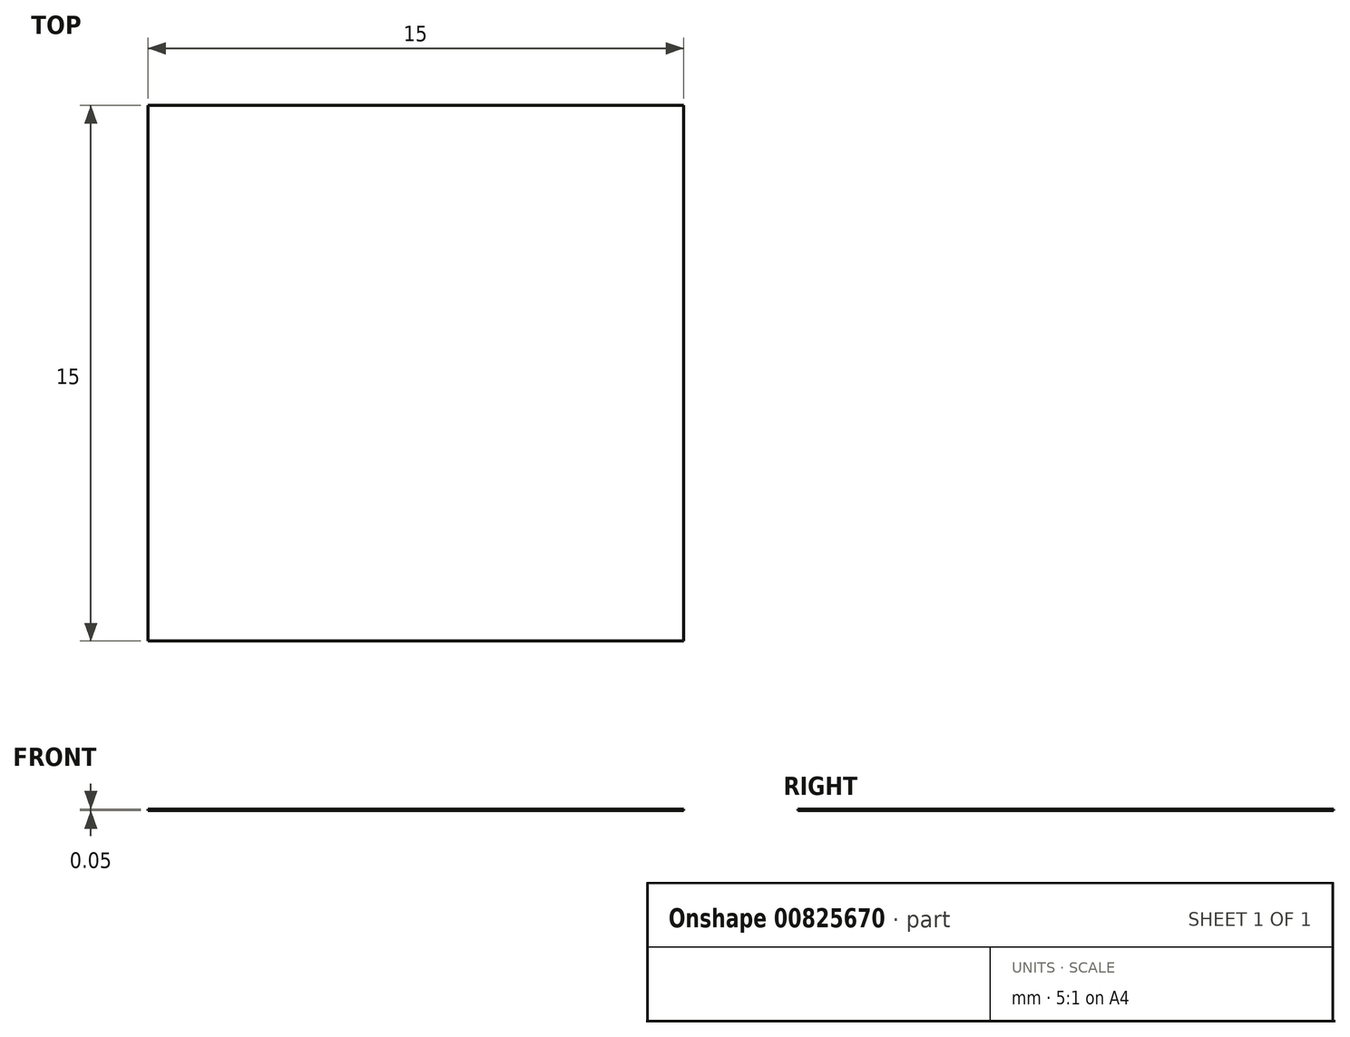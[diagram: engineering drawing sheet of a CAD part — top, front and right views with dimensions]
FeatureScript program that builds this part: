
annotation { "Feature Type Name" : "Feature", "Feature Type Description" : "" }
export const myFeature = defineFeature(function(context is Context, id is Id, definition is map)
    precondition{}
    {
        {
            var Q0;
            Q0=qCreatedBy(makeId("Top.planeOp"),FACE);
            var sketch = newSketch(context, id + "F0", { "sketchPlane" : qUnion([Q0])});
            skLineSegment(sketch, "E0.bottom", {"start": v(-18.19, 6.59) * mm, "end": v(-3.19, 6.59) * mm});
            skLineSegment(sketch, "E0.top", {"start": v(-18.19, -8.41) * mm, "end": v(-3.19, -8.41) * mm});
            skLineSegment(sketch, "E0.left", {"start": v(-18.19, 6.59) * mm, "end": v(-18.19, -8.41) * mm});
            skLineSegment(sketch, "E0.right", {"start": v(-3.19, 6.59) * mm, "end": v(-3.19, -8.41) * mm});
            skSolve(sketch);
        }
        {
            var Q0;
            Q0=makeQuery(id+"F0.imprint","IMPRINT",FACE,{"disambiguationData":[TD([[makeQuery(id+"F0.imprint","IMPRINT",EDGE,{"derivedFrom":sQuery(id+"F0.wireOp",EDGE,"E0.bottom")}),-1.0]])]});
            extrude(context, id + "F1", {"entities" : qUnion([Q0]), "depth" : 0.05 * mm, "offsetDistance" : 25 * mm});
        }
    });
